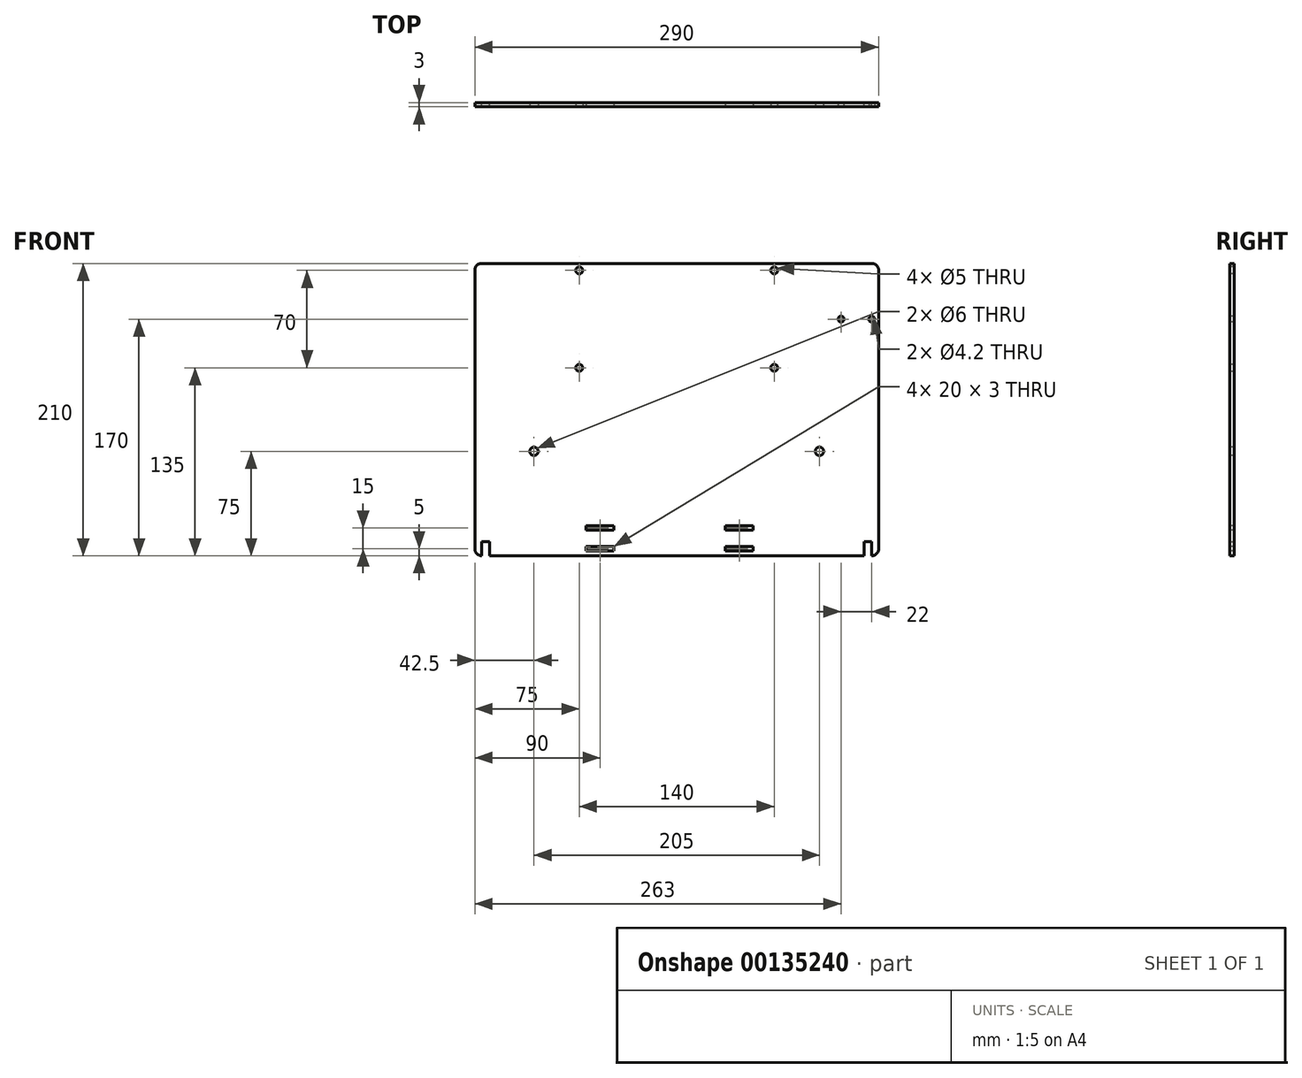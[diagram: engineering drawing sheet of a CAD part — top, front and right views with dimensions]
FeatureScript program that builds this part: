
annotation { "Feature Type Name" : "Feature", "Feature Type Description" : "" }
export const myFeature = defineFeature(function(context is Context, id is Id, definition is map)
    precondition{}
    {
        {
            var Q0;
            Q0=qCreatedBy(makeId("Front.planeOp"),FACE);
            var sketch = newSketch(context, id + "F0", { "sketchPlane" : qUnion([Q0])});
            skLineSegment(sketch, "E0.bottom", {"start": v(145, -105) * mm, "end": v(140, -105) * mm});
            skLineSegment(sketch, "E0.top", {"start": v(145, 105) * mm, "end": v(-145, 105) * mm});
            skLineSegment(sketch, "E0.left", {"start": v(145, -105) * mm, "end": v(145, 105) * mm});
            skLineSegment(sketch, "E0.right", {"start": v(-145, -105) * mm, "end": v(-145, 105) * mm});
            skPoint(sketch, "E0.middle", {"position": v(0, 0) * mm});
            skLineSegment(sketch, "E1", {"start": v(-140, -105) * mm, "end": v(-140, -95) * mm});
            skLineSegment(sketch, "E2", {"start": v(-140, -95) * mm, "end": v(-134.5, -95) * mm});
            skLineSegment(sketch, "E3", {"start": v(-134.5, -95) * mm, "end": v(-134.5, -105) * mm});
            skLineSegment(sketch, "E4", {"start": v(140, -105) * mm, "end": v(140, -95) * mm});
            skLineSegment(sketch, "E5", {"start": v(140, -95) * mm, "end": v(134.5, -95) * mm});
            skLineSegment(sketch, "E6", {"start": v(134.5, -95) * mm, "end": v(134.5, -105) * mm});
            skLineSegment(sketch, "E7.trimOffspring", {"start": v(-140, -105) * mm, "end": v(-145, -105) * mm});
            skLineSegment(sketch, "E8.trimOffspring", {"start": v(134.5, -105) * mm, "end": v(-134.5, -105) * mm});
            skSolve(sketch);
        }
        {
            var Q0;
            Q0=makeQuery(id+"F0.imprint","IMPRINT",FACE,{"disambiguationData":[TD([[makeQuery(id+"F0.imprint","IMPRINT",EDGE,{"derivedFrom":sQuery(id+"F0.wireOp",EDGE,"E0.bottom")}),-1.0]])]});
            extrude(context, id + "F1", {"entities" : qUnion([Q0]), "depth" : 3 * mm});
        }
        {
            var Q0;
            {var subQ0=sQuery(id+"F0.wireOp",EDGE,"E8.trimOffspring");var subQ1=sQuery(id+"F0.wireOp",EDGE,"E3");var subQ2=sQuery(id+"F0.wireOp",EDGE,"E4");var subQ3=sQuery(id+"F0.wireOp",EDGE,"E0.left");var subQ4=sQuery(id+"F0.wireOp",EDGE,"E0.bottom");var subQ5=sQuery(id+"F0.wireOp",EDGE,"E0.top");var subQ6=sQuery(id+"F0.wireOp",EDGE,"E7.trimOffspring");var subQ7=sQuery(id+"F0.wireOp",EDGE,"E0.right");var subQ8=sQuery(id+"F0.wireOp",EDGE,"E2");var subQ9=sQuery(id+"F0.wireOp",EDGE,"E1");var subQ10=sQuery(id+"F0.wireOp",EDGE,"E5");var subQ11=sQuery(id+"F0.wireOp",EDGE,"E6");Q0=makeQuery(id+"Fkeax6t5Ps2Em87_1.boolean.opBoolean","SPLIT",FACE,{"disambiguationData":[TD([makeQuery(id+"F1.opExtrude","SWEPT_FACE",FACE,{"disambiguationData":[OSD([subQ4])]})])],"derivedFrom":makeQuery(id+"F1.opExtrude","CAP_FACE",FACE,{"disambiguationData":[OSD([subQ4,subQ5,subQ3,subQ7,subQ9,subQ8,subQ1,subQ2,subQ10,subQ11,subQ6,subQ0])],"isStart":false})});}
            var sketch = newSketch(context, id + "F2", { "sketchPlane" : qUnion([Q0])});
            skCircle(sketch, "E9", {"center": v(-70, 100) * mm, "radius": 2.5 * mm});
            skCircle(sketch, "E10", {"center": v(-70, 30) * mm, "radius": 2.5 * mm});
            skCircle(sketch, "E11", {"center": v(70, 100) * mm, "radius": 2.5 * mm});
            skCircle(sketch, "E12", {"center": v(70, 30) * mm, "radius": 2.5 * mm});
            skSolve(sketch);
        }
        {
            var Q0;
            Q0 = qSketchRegion(id + "F2", true);
            extrude(context, id + "F3", {"entities" : qUnion([Q0]), "operationType" : NewBodyOperationType.REMOVE, "endBound" : BoundingType.UP_TO_NEXT, "oppositeDirection" : true, "depth" : 25 * mm});
        }
        {
            var Q0;
            {var subQ0=sQuery(id+"F0.wireOp",EDGE,"E0.left");var subQ1=sQuery(id+"F0.wireOp",EDGE,"E0.bottom");var subQ2=sQuery(id+"F0.wireOp",EDGE,"E0.right");var subQ3=sQuery(id+"F0.wireOp",EDGE,"E0.top");Q0=makeQuery(id+"Fkeax6t5Ps2Em87_1.boolean.opBoolean","SPLIT",FACE,{"disambiguationData":[TD([makeQuery(id+"F1.opExtrude","SWEPT_FACE",FACE,{"disambiguationData":[OSD([subQ1])]})])],"derivedFrom":makeQuery(id+"F1.opExtrude","CAP_FACE",FACE,{"disambiguationData":[OSD([subQ1,subQ3,subQ0,subQ2])],"isStart":false})});}
            var sketch = newSketch(context, id + "F4", { "sketchPlane" : qUnion([Q0])});
            skCircle(sketch, "E13", {"center": v(102.5, -30) * mm, "radius": 3 * mm});
            skCircle(sketch, "E14", {"center": v(-102.5, -30) * mm, "radius": 3 * mm});
            skSolve(sketch);
        }
        {
            var Q0;
            Q0=qSketchRegion(id+"F4",true);
            extrude(context, id + "F5", {"entities" : qUnion([Q0]), "operationType" : NewBodyOperationType.REMOVE, "endBound" : BoundingType.UP_TO_NEXT, "oppositeDirection" : true, "depth" : 25 * mm});
        }
        {
            var Q0;
            {var subQ0=sQuery(id+"F0.wireOp",EDGE,"E8.trimOffspring");var subQ1=sQuery(id+"F0.wireOp",EDGE,"E3");var subQ2=sQuery(id+"F0.wireOp",EDGE,"E4");var subQ3=sQuery(id+"F0.wireOp",EDGE,"E0.left");var subQ4=sQuery(id+"F0.wireOp",EDGE,"E0.bottom");var subQ5=sQuery(id+"F0.wireOp",EDGE,"E0.top");var subQ6=sQuery(id+"F0.wireOp",EDGE,"E7.trimOffspring");var subQ7=sQuery(id+"F0.wireOp",EDGE,"E0.right");var subQ8=sQuery(id+"F0.wireOp",EDGE,"E2");var subQ9=sQuery(id+"F0.wireOp",EDGE,"E1");var subQ10=sQuery(id+"F0.wireOp",EDGE,"E5");var subQ11=sQuery(id+"F0.wireOp",EDGE,"E6");Q0=makeQuery(id+"Fkeax6t5Ps2Em87_1.boolean.opBoolean","SPLIT",FACE,{"disambiguationData":[TD([makeQuery(id+"F1.opExtrude","SWEPT_FACE",FACE,{"disambiguationData":[OSD([subQ4])]})])],"derivedFrom":makeQuery(id+"F1.opExtrude","CAP_FACE",FACE,{"disambiguationData":[OSD([subQ4,subQ5,subQ3,subQ7,subQ9,subQ8,subQ1,subQ2,subQ10,subQ11,subQ6,subQ0])],"isStart":false})});}
            var sketch = newSketch(context, id + "F6", { "sketchPlane" : qUnion([Q0])});
            skCircle(sketch, "E15", {"center": v(118, 65) * mm, "radius": 2.1 * mm});
            skCircle(sketch, "E16", {"center": v(140, 65) * mm, "radius": 2.1 * mm});
            skSolve(sketch);
        }
        {
            var Q0;
            Q0 = qSketchRegion(id + "F6", true);
            extrude(context, id + "F7", {"entities" : qUnion([Q0]), "operationType" : NewBodyOperationType.REMOVE, "endBound" : BoundingType.UP_TO_NEXT, "oppositeDirection" : true, "depth" : 25 * mm});
        }
        {
            var Q0;
            Q0=makeQuery(id+"F1.opExtrude","CAP_FACE",FACE,{"disambiguationData":[OSD([sQuery(id+"F0.wireOp",EDGE,"E0.bottom"),sQuery(id+"F0.wireOp",EDGE,"E0.top"),sQuery(id+"F0.wireOp",EDGE,"E0.left"),sQuery(id+"F0.wireOp",EDGE,"E0.right"),sQuery(id+"F0.wireOp",EDGE,"E1"),sQuery(id+"F0.wireOp",EDGE,"E2"),sQuery(id+"F0.wireOp",EDGE,"E3"),sQuery(id+"F0.wireOp",EDGE,"E4"),sQuery(id+"F0.wireOp",EDGE,"E5"),sQuery(id+"F0.wireOp",EDGE,"E6"),sQuery(id+"F0.wireOp",EDGE,"E7.trimOffspring"),sQuery(id+"F0.wireOp",EDGE,"E8.trimOffspring")])],"isStart":false});
            var sketch = newSketch(context, id + "F8", { "sketchPlane" : qUnion([Q0])});
            skLineSegment(sketch, "E17.bottom", {"start": v(-45, -86.5) * mm, "end": v(-65, -86.5) * mm});
            skLineSegment(sketch, "E17.top", {"start": v(-45, -83.5) * mm, "end": v(-65, -83.5) * mm});
            skLineSegment(sketch, "E17.left", {"start": v(-45, -86.5) * mm, "end": v(-45, -83.5) * mm});
            skLineSegment(sketch, "E17.right", {"start": v(-65, -86.5) * mm, "end": v(-65, -83.5) * mm});
            skPoint(sketch, "E17.middle", {"position": v(-55, -85) * mm});
            skLineSegment(sketch, "E18.top", {"start": v(55, -83.5) * mm, "end": v(35, -83.5) * mm});
            skLineSegment(sketch, "E18.left", {"start": v(55, -86.5) * mm, "end": v(55, -83.5) * mm});
            skLineSegment(sketch, "E18.right", {"start": v(35, -86.5) * mm, "end": v(35, -83.5) * mm});
            skPoint(sketch, "E18.middle", {"position": v(45, -85) * mm});
            skPoint(sketch, "E18.cornerSnap0", {"position": v(-55, -86.5) * mm});
            skLineSegment(sketch, "E19.bottom", {"start": v(55, -101.5) * mm, "end": v(35, -101.5) * mm});
            skLineSegment(sketch, "E19.top", {"start": v(55, -98.5) * mm, "end": v(35, -98.5) * mm});
            skLineSegment(sketch, "E19.left", {"start": v(55, -101.5) * mm, "end": v(55, -98.5) * mm});
            skLineSegment(sketch, "E19.right", {"start": v(35, -101.5) * mm, "end": v(35, -98.5) * mm});
            skPoint(sketch, "E19.middle", {"position": v(45, -100) * mm});
            skLineSegment(sketch, "E20.bottom", {"start": v(-45, -98.5) * mm, "end": v(-65, -98.5) * mm});
            skLineSegment(sketch, "E20.top", {"start": v(-45, -101.5) * mm, "end": v(-65, -101.5) * mm});
            skLineSegment(sketch, "E20.left", {"start": v(-45, -98.5) * mm, "end": v(-45, -101.5) * mm});
            skLineSegment(sketch, "E20.right", {"start": v(-65, -98.5) * mm, "end": v(-65, -101.5) * mm});
            skPoint(sketch, "E20.middle", {"position": v(-55, -100) * mm});
            skLineSegment(sketch, "E21", {"start": v(35, -86.5) * mm, "end": v(55, -86.5) * mm});
            skSolve(sketch);
        }
        {
            var Q0;
            Q0 = qSketchRegion(id + "F8", true);
            extrude(context, id + "F9", {"entities" : qUnion([Q0]), "operationType" : NewBodyOperationType.REMOVE, "endBound" : BoundingType.UP_TO_NEXT, "oppositeDirection" : true, "depth" : 25 * mm});
        }
        {
            var Q0;
            Q0=makeQuery(id+"F1.opExtrude","SWEPT_EDGE",EDGE,{"disambiguationData":[OSD([sQuery(id+"F0.wireOp",EDGE,"E0.top"),sQuery(id+"F0.wireOp",EDGE,"E0.right")])]});
            var Q1;
            Q1=makeQuery(id+"F1.opExtrude","SWEPT_EDGE",EDGE,{"disambiguationData":[OSD([sQuery(id+"F0.wireOp",EDGE,"E0.right"),sQuery(id+"F0.wireOp",EDGE,"E7.trimOffspring")])]});
            var Q2;
            Q2=makeQuery(id+"F1.opExtrude","SWEPT_EDGE",EDGE,{"disambiguationData":[OSD([sQuery(id+"F0.wireOp",EDGE,"E0.bottom"),sQuery(id+"F0.wireOp",EDGE,"E0.left")])]});
            var Q3;
            Q3=makeQuery(id+"F1.opExtrude","SWEPT_EDGE",EDGE,{"disambiguationData":[OSD([sQuery(id+"F0.wireOp",EDGE,"E0.top"),sQuery(id+"F0.wireOp",EDGE,"E0.left")])]});
            fillet(context, id + "F10", {"entities" : qUnion([Q0, Q1, Q2, Q3]), "radius" : 5 * mm, "tangentPropagation" : true, "allowEdgeOverflow" : false});
        }
    });
